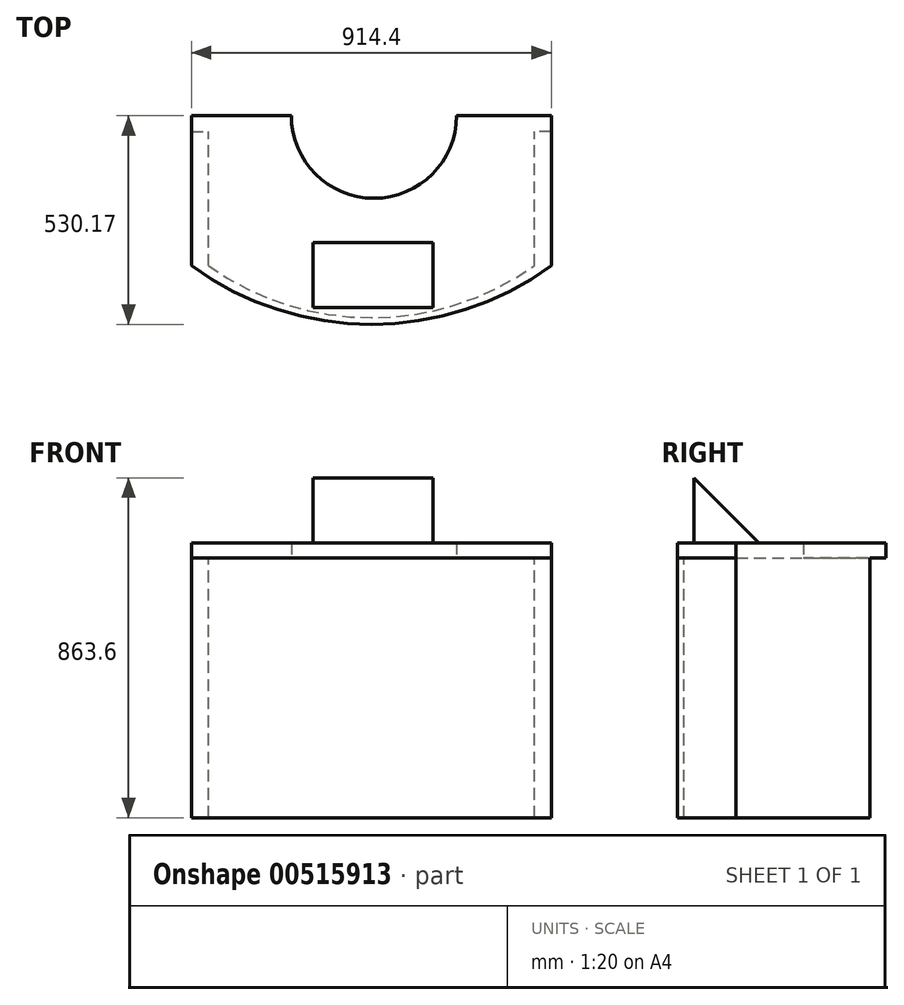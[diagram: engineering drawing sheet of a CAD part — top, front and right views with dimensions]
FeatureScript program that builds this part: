
annotation { "Feature Type Name" : "Feature", "Feature Type Description" : "" }
export const myFeature = defineFeature(function(context is Context, id is Id, definition is map)
    precondition{}
    {
        {
            var Q0;
            Q0=qCreatedBy(makeId("Top.planeOp"),FACE);
            var sketch = newSketch(context, id + "F0", { "sketchPlane" : qUnion([Q0])});
            skLineSegment(sketch, "E0.bottom", {"start": v(-448.63, 122.89) * mm, "end": v(-194.82, 122.89) * mm});
            skLineSegment(sketch, "E0.left", {"start": v(-448.63, 122.89) * mm, "end": v(-448.63, -258.11) * mm});
            skLineSegment(sketch, "E0.right", {"start": v(465.77, 122.89) * mm, "end": v(465.77, -258.11) * mm});
            skArc(sketch, "E1", {"start": v(-448.63, -258.11) * mm, "mid": v(8.57, -407.28) * mm, "end": v(465.77, -258.11) * mm});
            skArc(sketch, "E2", {"start": v(-194.82, 122.89) * mm, "mid": v(14.97, -86.9) * mm, "end": v(224.77, 122.89) * mm});
            skLineSegment(sketch, "E3.trimOffspring", {"start": v(224.77, 122.89) * mm, "end": v(465.77, 122.89) * mm});
            skSolve(sketch);
        }
        {
            var Q0;
            Q0 = qSketchRegion(id + "F0", true);
            extrude(context, id + "F1", {"entities" : qUnion([Q0]), "depth" : 38.1 * mm, "offsetDistance" : 25.4 * mm});
        }
        {
            var Q0;
            Q0=makeQuery(id+"F1.opExtrude","CAP_FACE",FACE,{"disambiguationData":[OSD([sQuery(id+"F0.wireOp",EDGE,"E0.bottom"),sQuery(id+"F0.wireOp",EDGE,"E0.left"),sQuery(id+"F0.wireOp",EDGE,"E0.right"),sQuery(id+"F0.wireOp",EDGE,"E1"),sQuery(id+"F0.wireOp",EDGE,"E2"),sQuery(id+"F0.wireOp",EDGE,"E3.trimOffspring")])],"isStart":true});
            var sketch = newSketch(context, id + "F2", { "sketchPlane" : qUnion([Q0])});
            skLineSegment(sketch, "E4.top", {"start": v(465.77, -82.4) * mm, "end": v(422.6, -82.4) * mm});
            skLineSegment(sketch, "E4.left", {"start": v(465.77, 258.11) * mm, "end": v(465.77, -82.4) * mm});
            skLineSegment(sketch, "E4.right", {"start": v(422.6, 258.11) * mm, "end": v(422.6, -82.4) * mm});
            skLineSegment(sketch, "E5.top", {"start": v(-448.63, -82.4) * mm, "end": v(-405.45, -82.4) * mm});
            skLineSegment(sketch, "E5.left", {"start": v(-448.63, 258.11) * mm, "end": v(-448.63, -82.4) * mm});
            skLineSegment(sketch, "E5.right", {"start": v(-405.45, 258.11) * mm, "end": v(-405.45, -82.4) * mm});
            skArc(sketch, "E6", {"start": v(465.77, 258.11) * mm, "mid": v(8.57, 406.68) * mm, "end": v(-448.63, 258.11) * mm});
            skArc(sketch, "E7", {"start": v(422.6, 258.11) * mm, "mid": v(8.57, 390.26) * mm, "end": v(-405.45, 258.11) * mm});
            skSolve(sketch);
        }
        {
            var Q0;
            Q0 = qSketchRegion(id + "F2", true);
            extrude(context, id + "F3", {"entities" : qUnion([Q0]), "operationType" : NewBodyOperationType.ADD, "depth" : 660.4 * mm, "offsetDistance" : 25.4 * mm});
        }
        {
            var Q0;
            Q0=makeQuery(id+"F1.opExtrude","CAP_FACE",FACE,{"disambiguationData":[OSD([sQuery(id+"F0.wireOp",EDGE,"E0.bottom"),sQuery(id+"F0.wireOp",EDGE,"E0.left"),sQuery(id+"F0.wireOp",EDGE,"E0.right"),sQuery(id+"F0.wireOp",EDGE,"E1"),sQuery(id+"F0.wireOp",EDGE,"E2"),sQuery(id+"F0.wireOp",EDGE,"E3.trimOffspring")])],"isStart":false});
            var sketch = newSketch(context, id + "F4", { "sketchPlane" : qUnion([Q0])});
            skLineSegment(sketch, "E8.bottom", {"start": v(164.74, -364.65) * mm, "end": v(-140.06, -364.65) * mm});
            skLineSegment(sketch, "E8.top", {"start": v(164.74, -199.55) * mm, "end": v(-140.06, -199.55) * mm});
            skLineSegment(sketch, "E8.left", {"start": v(164.74, -364.65) * mm, "end": v(164.74, -199.55) * mm});
            skLineSegment(sketch, "E8.right", {"start": v(-140.06, -364.65) * mm, "end": v(-140.06, -199.55) * mm});
            skSolve(sketch);
        }
        {
            var Q0;
            Q0 = qSketchRegion(id + "F4", true);
            extrude(context, id + "F5", {"entities" : qUnion([Q0]), "operationType" : NewBodyOperationType.ADD, "depth" : 203.2 * mm, "offsetDistance" : 25.4 * mm});
        }
        {
            var Q0;
            Q0=makeQuery(id+"F5.opExtrude","CAP_EDGE",EDGE,{"disambiguationData":[OSD([sQuery(id+"F4.wireOp",EDGE,"E8.top")])],"isStart":false});
            chamfer(context, id + "F6", {"entities" : qUnion([Q0]), "width" : 203.2 * mm, "tangentPropagation" : true});
        }
    });
